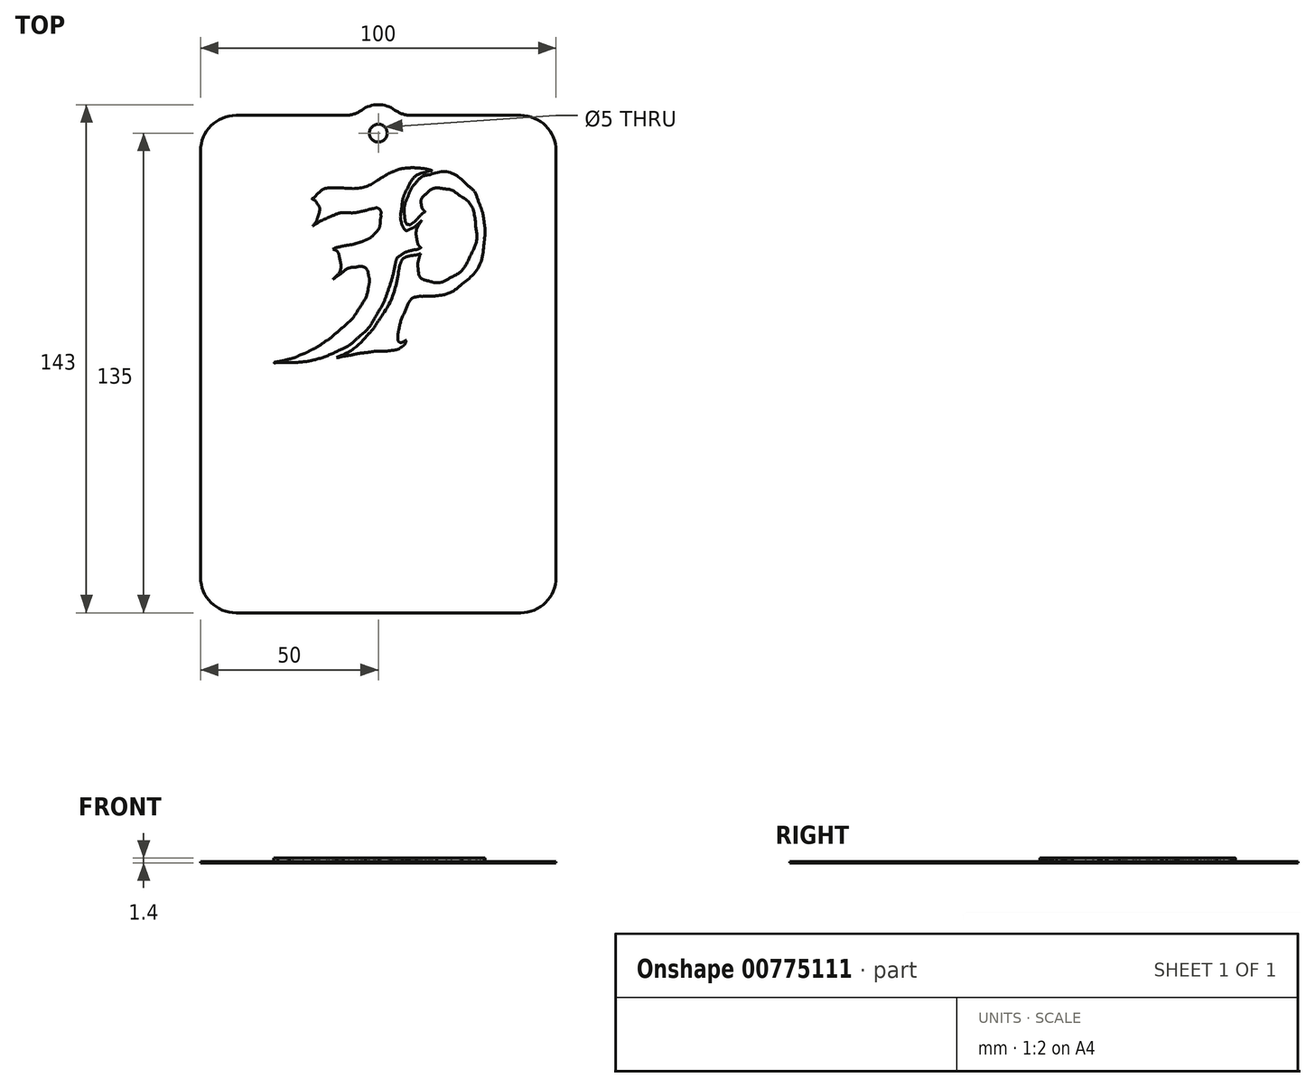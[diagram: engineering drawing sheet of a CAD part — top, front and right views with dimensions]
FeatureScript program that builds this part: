
annotation { "Feature Type Name" : "Feature", "Feature Type Description" : "" }
export const myFeature = defineFeature(function(context is Context, id is Id, definition is map)
    precondition{}
    {
        {
            var Q0;
            Q0=qCreatedBy(makeId("Top.planeOp"),FACE);
            var sketch = newSketch(context, id + "F0", { "sketchPlane" : qUnion([Q0])});
            skLineSegment(sketch, "E0.bottom", {"start": v(-40, 70) * mm, "end": v(-9.33, 70) * mm});
            skLineSegment(sketch, "E0.top", {"start": v(-40, -70) * mm, "end": v(40, -70) * mm});
            skLineSegment(sketch, "E0.left", {"start": v(-50, 60) * mm, "end": v(-50, -60) * mm});
            skLineSegment(sketch, "E0.right", {"start": v(50, 60) * mm, "end": v(50, -60) * mm});
            skPoint(sketch, "E0.middle", {"position": v(0, 0) * mm});
            skCircle(sketch, "E1", {"center": v(0, 65) * mm, "radius": 2.5 * mm});
            skPoint(sketch, "E2.visualSharp", {"position": v(-50, 70) * mm});
            skArc(sketch, "E2.filletArc", {"start": v(-40, 70) * mm, "mid": v(-47.07, 67.07) * mm, "end": v(-50, 60) * mm});
            skPoint(sketch, "E3.visualSharp", {"position": v(50, 70) * mm});
            skArc(sketch, "E3.filletArc", {"start": v(50, 60) * mm, "mid": v(47.07, 67.07) * mm, "end": v(40, 70) * mm});
            skPoint(sketch, "E4.visualSharp", {"position": v(50, -70) * mm});
            skArc(sketch, "E4.filletArc", {"start": v(40, -70) * mm, "mid": v(47.07, -67.07) * mm, "end": v(50, -60) * mm});
            skPoint(sketch, "E5.visualSharp", {"position": v(-50, -70) * mm});
            skArc(sketch, "E5.filletArc", {"start": v(-50, -60) * mm, "mid": v(-47.07, -67.07) * mm, "end": v(-40, -70) * mm});
            skArc(sketch, "E6", {"start": v(-4.66, 71.5) * mm, "mid": v(0, 73) * mm, "end": v(4.66, 71.5) * mm});
            skArc(sketch, "E7.filletArc", {"start": v(-9.33, 70) * mm, "mid": v(-6.88, 70.38) * mm, "end": v(-4.66, 71.5) * mm});
            skLineSegment(sketch, "E8", {"start": v(40, 70) * mm, "end": v(9.33, 70) * mm});
            skArc(sketch, "E9.filletArc", {"start": v(4.66, 71.5) * mm, "mid": v(6.88, 70.38) * mm, "end": v(9.33, 70) * mm});
            skSolve(sketch);
        }
        {
            var Q0;
            Q0=qSketchRegion(id+"F0",true);
            extrude(context, id + "F1", {"entities" : qUnion([Q0]), "depth" : .4 * mm, "offsetDistance" : 25 * mm, "symmetric" : true});
        }
        {
            var Q0;
            Q0=makeQuery(id+"F1.opExtrude","CAP_FACE",FACE,{"disambiguationData":[OSD([sQuery(id+"F0.wireOp",EDGE,"E0.bottom"),sQuery(id+"F0.wireOp",EDGE,"E0.top"),sQuery(id+"F0.wireOp",EDGE,"E0.left"),sQuery(id+"F0.wireOp",EDGE,"E0.right"),sQuery(id+"F0.wireOp",EDGE,"E1"),sQuery(id+"F0.wireOp",EDGE,"E2.filletArc"),sQuery(id+"F0.wireOp",EDGE,"E3.filletArc"),sQuery(id+"F0.wireOp",EDGE,"E4.filletArc"),sQuery(id+"F0.wireOp",EDGE,"E5.filletArc"),sQuery(id+"F0.wireOp",EDGE,"E6"),sQuery(id+"F0.wireOp",EDGE,"E7.filletArc"),sQuery(id+"F0.wireOp",EDGE,"E8"),sQuery(id+"F0.wireOp",EDGE,"E9.filletArc")])],"isStart":false});
            var sketch = newSketch(context, id + "F2", { "sketchPlane" : qUnion([Q0])});
            skFitSpline(sketch, "E10", {"points": [v(10.1, 55.33) * mm, v(10.4, 55.2) * mm, v(10.72, 55.22) * mm, v(11.03, 55.2) * mm]});
            skFitSpline(sketch, "E11", {"points": [v(11.03, 55.2) * mm, v(12.3, 55.1) * mm, v(13.56, 54.92) * mm, v(14.79, 54.6) * mm]});
            skFitSpline(sketch, "E12", {"points": [v(14.79, 54.6) * mm, v(14.9, 54.58) * mm, v(15.03, 54.59) * mm, v(15.1, 54.42) * mm]});
            skFitSpline(sketch, "E13", {"points": [v(15.1, 54.42) * mm, v(14.4, 54.4) * mm, v(13.76, 54.2) * mm, v(13.12, 53.98) * mm]});
            skFitSpline(sketch, "E14", {"points": [v(13.12, 53.98) * mm, v(10.8, 53.17) * mm, v(9.24, 51.53) * mm, v(8.14, 49.38) * mm]});
            skFitSpline(sketch, "E15", {"points": [v(8.14, 49.38) * mm, v(7.37, 47.87) * mm, v(6.84, 46.27) * mm, v(6.63, 44.6) * mm]});
            skFitSpline(sketch, "E16", {"points": [v(6.63, 44.6) * mm, v(6.43, 42.98) * mm, v(6.2, 41.35) * mm, v(6.52, 39.72) * mm]});
            skFitSpline(sketch, "E17", {"points": [v(6.52, 39.72) * mm, v(6.57, 39.43) * mm, v(6.65, 39.15) * mm, v(6.8, 38.88) * mm]});
            skFitSpline(sketch, "E18", {"points": [v(6.8, 38.88) * mm, v(7.2, 38.14) * mm, v(7.82, 37.59) * mm, v(8.94, 38.03) * mm]});
            skFitSpline(sketch, "E19", {"points": [v(8.94, 38.03) * mm, v(9.92, 38.4) * mm, v(10.73, 39.03) * mm, v(11.49, 39.74) * mm]});
            skFitSpline(sketch, "E20", {"points": [v(11.49, 39.74) * mm, v(11.7, 39.93) * mm, v(11.87, 40.14) * mm, v(12.1, 40.4) * mm]});
            skFitSpline(sketch, "E21", {"points": [v(12.1, 40.4) * mm, v(12.11, 40.2) * mm, v(12, 40.11) * mm, v(11.95, 40.02) * mm]});
            skFitSpline(sketch, "E22", {"points": [v(11.95, 40.02) * mm, v(10.86, 38.25) * mm, v(10.65, 36.34) * mm, v(11, 34.33) * mm]});
            skFitSpline(sketch, "E23", {"points": [v(11, 34.33) * mm, v(11.1, 33.86) * mm, v(11.3, 33.44) * mm, v(11.66, 33.1) * mm]});
            skFitSpline(sketch, "E24", {"points": [v(11.66, 33.1) * mm, v(12.01, 32.76) * mm, v(12, 32.75) * mm, v(11.54, 32.55) * mm]});
            skFitSpline(sketch, "E25", {"points": [v(11.54, 32.55) * mm, v(10.9, 32.27) * mm, v(10.2, 32.2) * mm, v(9.52, 32.03) * mm]});
            skFitSpline(sketch, "E26", {"points": [v(9.52, 32.03) * mm, v(8.35, 31.74) * mm, v(7.24, 31.29) * mm, v(6.24, 30.59) * mm]});
            skFitSpline(sketch, "E27", {"points": [v(6.24, 30.59) * mm, v(5.4, 30) * mm, v(4.98, 29.14) * mm, v(4.78, 28.18) * mm]});
            skFitSpline(sketch, "E28", {"points": [v(4.78, 28.18) * mm, v(4.29, 25.78) * mm, v(3.65, 23.42) * mm, v(2.86, 21.1) * mm]});
            skFitSpline(sketch, "E29", {"points": [v(2.86, 21.1) * mm, v(2.18, 19.1) * mm, v(1.4, 17.13) * mm, v(0.35, 15.3) * mm]});
            skFitSpline(sketch, "E30", {"points": [v(0.35, 15.3) * mm, v(-1.13, 12.75) * mm, v(-2.67, 10.25) * mm, v(-4.86, 8.23) * mm]});
            skFitSpline(sketch, "E31", {"points": [v(-4.86, 8.23) * mm, v(-6.57, 6.66) * mm, v(-8.36, 5.17) * mm, v(-10.46, 4.16) * mm]});
            skFitSpline(sketch, "E32", {"points": [v(-10.46, 4.16) * mm, v(-13.06, 2.91) * mm, v(-15.74, 1.83) * mm, v(-18.53, 1.11) * mm]});
            skFitSpline(sketch, "E33", {"points": [v(-18.53, 1.11) * mm, v(-19.7, 0.81) * mm, v(-20.9, 0.68) * mm, v(-22.09, 0.56) * mm]});
            skFitSpline(sketch, "E34", {"points": [v(-22.09, 0.56) * mm, v(-23.04, 0.46) * mm, v(-24, 0.4) * mm, v(-24.95, 0.4) * mm]});
            skFitSpline(sketch, "E35", {"points": [v(-26.63, 0.4) * mm, v(-26.77, 0.4) * mm, v(-26.91, 0.4) * mm, v(-27.05, 0.4) * mm]});
            skFitSpline(sketch, "E36", {"points": [v(-29.43, 0.48) * mm, v(-28.15, 0.72) * mm, v(-26.87, 0.96) * mm, v(-25.61, 1.3) * mm]});
            skFitSpline(sketch, "E37", {"points": [v(-25.61, 1.3) * mm, v(-25.1, 1.42) * mm, v(-24.59, 1.52) * mm, v(-24.09, 1.67) * mm]});
            skFitSpline(sketch, "E38", {"points": [v(-24.09, 1.67) * mm, v(-23.09, 1.97) * mm, v(-22.19, 2.52) * mm, v(-21.2, 2.87) * mm]});
            skFitSpline(sketch, "E39", {"points": [v(-21.2, 2.87) * mm, v(-20.16, 3.24) * mm, v(-19.2, 3.81) * mm, v(-18.21, 4.3) * mm]});
            skFitSpline(sketch, "E40", {"points": [v(-18.21, 4.3) * mm, v(-16.92, 4.96) * mm, v(-15.76, 5.8) * mm, v(-14.56, 6.58) * mm]});
            skFitSpline(sketch, "E41", {"points": [v(-14.56, 6.58) * mm, v(-13.45, 7.32) * mm, v(-12.44, 8.2) * mm, v(-11.43, 9.09) * mm]});
            skFitSpline(sketch, "E42", {"points": [v(-11.43, 9.09) * mm, v(-9.34, 10.92) * mm, v(-7.3, 12.82) * mm, v(-5.74, 15.18) * mm]});
            skFitSpline(sketch, "E43", {"points": [v(-5.74, 15.18) * mm, v(-4.42, 17.2) * mm, v(-3.27, 19.3) * mm, v(-2.77, 21.72) * mm]});
            skFitSpline(sketch, "E44", {"points": [v(-2.77, 21.72) * mm, v(-2.57, 22.7) * mm, v(-2.47, 23.74) * mm, v(-2.72, 24.7) * mm]});
            skFitSpline(sketch, "E45", {"points": [v(-2.72, 24.7) * mm, v(-3.22, 26.66) * mm, v(-4.56, 27.47) * mm, v(-6.5, 27.23) * mm]});
            skFitSpline(sketch, "E46", {"points": [v(-6.5, 27.23) * mm, v(-8.44, 27) * mm, v(-9.99, 25.93) * mm, v(-11.5, 24.8) * mm]});
            skFitSpline(sketch, "E47", {"points": [v(-11.5, 24.8) * mm, v(-11.87, 24.53) * mm, v(-12.22, 24.25) * mm, v(-12.58, 23.97) * mm]});
            skFitSpline(sketch, "E48", {"points": [v(-12.58, 23.97) * mm, v(-12.63, 24.07) * mm, v(-12.57, 24.1) * mm, v(-12.55, 24.12) * mm]});
            skFitSpline(sketch, "E49", {"points": [v(-12.55, 24.12) * mm, v(-10.9, 25.86) * mm, v(-10.5, 27.93) * mm, v(-11, 30.22) * mm]});
            skFitSpline(sketch, "E50", {"points": [v(-11, 30.22) * mm, v(-11.22, 31.21) * mm, v(-11.8, 31.93) * mm, v(-12.78, 32.35) * mm]});
            skFitSpline(sketch, "E51", {"points": [v(-12.78, 32.35) * mm, v(-12.15, 32.69) * mm, v(-11.5, 32.88) * mm, v(-10.84, 33.02) * mm]});
            skFitSpline(sketch, "E52", {"points": [v(-10.84, 33.02) * mm, v(-9.2, 33.39) * mm, v(-7.52, 33.62) * mm, v(-5.9, 34.09) * mm]});
            skFitSpline(sketch, "E53", {"points": [v(-5.9, 34.09) * mm, v(-5.03, 34.33) * mm, v(-4.2, 34.64) * mm, v(-3.37, 35) * mm]});
            skFitSpline(sketch, "E54", {"points": [v(-3.37, 35) * mm, v(-2.4, 35.43) * mm, v(-1.6, 36.08) * mm, v(-0.89, 36.86) * mm]});
            skFitSpline(sketch, "E55", {"points": [v(-0.89, 36.86) * mm, v(0.02, 37.85) * mm, v(0.46, 39.04) * mm, v(0.57, 40.38) * mm]});
            skFitSpline(sketch, "E56", {"points": [v(0.57, 40.38) * mm, v(0.61, 40.94) * mm, v(0.74, 41.5) * mm, v(0.7, 42.07) * mm]});
            skFitSpline(sketch, "E57", {"points": [v(0.7, 42.07) * mm, v(0.64, 43.16) * mm, v(-0.32, 43.94) * mm, v(-1.38, 43.77) * mm]});
            skFitSpline(sketch, "E58", {"points": [v(-1.38, 43.77) * mm, v(-2.44, 43.6) * mm, v(-3.48, 43.26) * mm, v(-4.53, 43.03) * mm]});
            skFitSpline(sketch, "E59", {"points": [v(-4.53, 43.03) * mm, v(-5.8, 42.75) * mm, v(-7.08, 42.56) * mm, v(-8.38, 42.58) * mm]});
            skFitSpline(sketch, "E60", {"points": [v(-8.38, 42.58) * mm, v(-10.34, 42.62) * mm, v(-12.17, 42.07) * mm, v(-13.95, 41.3) * mm]});
            skFitSpline(sketch, "E61", {"points": [v(-13.95, 41.3) * mm, v(-15.43, 40.68) * mm, v(-16.86, 39.94) * mm, v(-18.18, 39) * mm]});
            skFitSpline(sketch, "E62", {"points": [v(-18.18, 39) * mm, v(-18.24, 38.96) * mm, v(-18.3, 38.88) * mm, v(-18.43, 38.92) * mm]});
            skFitSpline(sketch, "E63", {"points": [v(-18.43, 38.92) * mm, v(-17.81, 39.62) * mm, v(-17.36, 40.41) * mm, v(-17.08, 41.27) * mm]});
            skFitSpline(sketch, "E64", {"points": [v(-17.08, 41.27) * mm, v(-16.6, 42.73) * mm, v(-16.57, 44.19) * mm, v(-17.45, 45.55) * mm]});
            skFitSpline(sketch, "E65", {"points": [v(-17.45, 45.55) * mm, v(-17.75, 46.02) * mm, v(-18.2, 46.27) * mm, v(-18.7, 46.56) * mm]});
            skFitSpline(sketch, "E66", {"points": [v(-18.7, 46.56) * mm, v(-17.86, 47.04) * mm, v(-17.27, 47.78) * mm, v(-16.56, 48.37) * mm]});
            skFitSpline(sketch, "E67", {"points": [v(-16.56, 48.37) * mm, v(-15.5, 49.26) * mm, v(-14.24, 49.56) * mm, v(-12.91, 49.6) * mm]});
            skFitSpline(sketch, "E68", {"points": [v(-12.91, 49.6) * mm, v(-11.9, 49.62) * mm, v(-10.88, 49.57) * mm, v(-9.87, 49.54) * mm]});
            skFitSpline(sketch, "E69", {"points": [v(-9.87, 49.54) * mm, v(-6.28, 49.43) * mm, v(-2.89, 50.17) * mm, v(0.23, 52.03) * mm]});
            skFitSpline(sketch, "E70", {"points": [v(0.23, 52.03) * mm, v(1.55, 52.82) * mm, v(2.87, 53.63) * mm, v(4.3, 54.22) * mm]});
            skFitSpline(sketch, "E71", {"points": [v(4.3, 54.22) * mm, v(5.65, 54.79) * mm, v(7.07, 55.1) * mm, v(8.53, 55.2) * mm]});
            skFitSpline(sketch, "E72", {"points": [v(8.53, 55.2) * mm, v(8.75, 55.21) * mm, v(8.98, 55.21) * mm, v(9.18, 55.33) * mm]});
            skFitSpline(sketch, "E73", {"points": [v(9.18, 55.33) * mm, v(9.2, 55.33) * mm, v(9.23, 55.33) * mm, v(9.25, 55.33) * mm]});
            skFitSpline(sketch, "E74", {"points": [v(9.95, 55.33) * mm, v(10, 55.33) * mm, v(10.05, 55.33) * mm, v(10.1, 55.33) * mm]});
            skFitSpline(sketch, "E75", {"points": [v(30, 35.94) * mm, v(29.82, 35.5) * mm, v(29.87, 35.05) * mm, v(29.8, 34.6) * mm]});
            skFitSpline(sketch, "E76", {"points": [v(29.8, 34.6) * mm, v(29.15, 29.83) * mm, v(27.18, 25.75) * mm, v(23.53, 22.6) * mm]});
            skFitSpline(sketch, "E77", {"points": [v(23.53, 22.6) * mm, v(21.48, 20.82) * mm, v(19.1, 19.7) * mm, v(16.43, 19.27) * mm]});
            skFitSpline(sketch, "E78", {"points": [v(16.43, 19.27) * mm, v(15.28, 19.08) * mm, v(14.1, 19.13) * mm, v(12.94, 19.09) * mm]});
            skFitSpline(sketch, "E79", {"points": [v(12.94, 19.09) * mm, v(12.19, 19.06) * mm, v(11.43, 19.06) * mm, v(10.68, 18.9) * mm]});
            skFitSpline(sketch, "E80", {"points": [v(10.68, 18.9) * mm, v(9.83, 18.73) * mm, v(9.19, 18.27) * mm, v(8.71, 17.55) * mm]});
            skFitSpline(sketch, "E81", {"points": [v(8.71, 17.55) * mm, v(8.55, 17.32) * mm, v(8.4, 17.08) * mm, v(8.3, 16.82) * mm]});
            skFitSpline(sketch, "E82", {"points": [v(8.3, 16.82) * mm, v(7.28, 14.4) * mm, v(6.28, 11.98) * mm, v(5.71, 9.41) * mm]});
            skFitSpline(sketch, "E83", {"points": [v(5.71, 9.41) * mm, v(5.58, 8.8) * mm, v(5.5, 8.18) * mm, v(5.54, 7.55) * mm]});
            skFitSpline(sketch, "E84", {"points": [v(5.54, 7.55) * mm, v(5.6, 6.54) * mm, v(6.29, 6.06) * mm, v(7.22, 6.4) * mm]});
            skFitSpline(sketch, "E85", {"points": [v(7.22, 6.4) * mm, v(7.42, 6.48) * mm, v(7.62, 6.57) * mm, v(7.85, 6.68) * mm]});
            skFitSpline(sketch, "E86", {"points": [v(7.85, 6.68) * mm, v(7.66, 5.99) * mm, v(7.35, 5.44) * mm, v(6.8, 5.02) * mm]});
            skFitSpline(sketch, "E87", {"points": [v(6.8, 5.02) * mm, v(5.85, 4.3) * mm, v(4.76, 3.97) * mm, v(3.6, 3.82) * mm]});
            skFitSpline(sketch, "E88", {"points": [v(3.6, 3.82) * mm, v(2.44, 3.67) * mm, v(1.28, 3.65) * mm, v(0.11, 3.61) * mm]});
            skFitSpline(sketch, "E89", {"points": [v(0.11, 3.61) * mm, v(-1.14, 3.57) * mm, v(-2.37, 3.38) * mm, v(-3.6, 3.23) * mm]});
            skFitSpline(sketch, "E90", {"points": [v(-3.6, 3.23) * mm, v(-5.73, 2.96) * mm, v(-7.8, 2.5) * mm, v(-9.92, 2.18) * mm]});
            skFitSpline(sketch, "E91", {"points": [v(-9.92, 2.18) * mm, v(-10.5, 2.1) * mm, v(-11.04, 1.9) * mm, v(-11.62, 1.83) * mm]});
            skFitSpline(sketch, "E92", {"points": [v(-11.77, 1.9) * mm, v(-8.29, 3.46) * mm, v(-5.3, 5.7) * mm, v(-2.71, 8.52) * mm]});
            skFitSpline(sketch, "E93", {"points": [v(-2.71, 8.52) * mm, v(-1.4, 9.95) * mm, v(-0.37, 11.54) * mm, v(0.65, 13.17) * mm]});
            skFitSpline(sketch, "E94", {"points": [v(0.65, 13.17) * mm, v(3.21, 17.28) * mm, v(4.83, 21.77) * mm, v(5.8, 26.51) * mm]});
            skFitSpline(sketch, "E95", {"points": [v(5.8, 26.51) * mm, v(5.93, 27.12) * mm, v(5.98, 27.75) * mm, v(6.26, 28.32) * mm]});
            skFitSpline(sketch, "E96", {"points": [v(6.26, 28.32) * mm, v(6.88, 29.6) * mm, v(7.97, 30.22) * mm, v(9.29, 30.53) * mm]});
            skFitSpline(sketch, "E97", {"points": [v(9.29, 30.53) * mm, v(9.52, 30.6) * mm, v(9.77, 30.6) * mm, v(10.01, 30.64) * mm]});
            skFitSpline(sketch, "E98", {"points": [v(10.01, 30.64) * mm, v(10.61, 30.72) * mm, v(11.2, 30.84) * mm, v(11.77, 31.12) * mm]});
            skFitSpline(sketch, "E99", {"points": [v(11.77, 31.12) * mm, v(11.8, 30.83) * mm, v(11.66, 30.62) * mm, v(11.6, 30.38) * mm]});
            skFitSpline(sketch, "E100", {"points": [v(11.6, 30.38) * mm, v(11.27, 29.13) * mm, v(11.08, 27.86) * mm, v(11.26, 26.56) * mm]});
            skFitSpline(sketch, "E101", {"points": [v(11.26, 26.56) * mm, v(11.5, 24.84) * mm, v(12.51, 23.84) * mm, v(14.16, 23.44) * mm]});
            skFitSpline(sketch, "E102", {"points": [v(14.16, 23.44) * mm, v(16.43, 22.88) * mm, v(18.55, 23.34) * mm, v(20.55, 24.47) * mm]});
            skFitSpline(sketch, "E103", {"points": [v(20.55, 24.47) * mm, v(22.99, 25.85) * mm, v(24.64, 27.97) * mm, v(25.87, 30.46) * mm]});
            skFitSpline(sketch, "E104", {"points": [v(25.87, 30.46) * mm, v(27.07, 32.92) * mm, v(27.75, 35.52) * mm, v(27.45, 38.26) * mm]});
            skFitSpline(sketch, "E105", {"points": [v(27.45, 38.26) * mm, v(27.05, 41.89) * mm, v(25.82, 45.16) * mm, v(22.85, 47.47) * mm]});
            skFitSpline(sketch, "E106", {"points": [v(22.85, 47.47) * mm, v(21.73, 48.34) * mm, v(20.48, 49.04) * mm, v(19.06, 49.25) * mm]});
            skFitSpline(sketch, "E107", {"points": [v(19.06, 49.25) * mm, v(16.96, 49.57) * mm, v(14.97, 49.26) * mm, v(13.33, 47.78) * mm]});
            skFitSpline(sketch, "E108", {"points": [v(13.33, 47.78) * mm, v(12.27, 46.82) * mm, v(12.02, 45.54) * mm, v(12.22, 44.15) * mm]});
            skFitSpline(sketch, "E109", {"points": [v(12.22, 44.15) * mm, v(12.25, 43.92) * mm, v(12.4, 43.72) * mm, v(12.57, 43.55) * mm]});
            skFitSpline(sketch, "E110", {"points": [v(12.57, 43.55) * mm, v(12.78, 43.32) * mm, v(13, 43.09) * mm, v(13.23, 42.85) * mm]});
            skFitSpline(sketch, "E111", {"points": [v(13.23, 42.85) * mm, v(12.52, 42.5) * mm, v(11.97, 41.95) * mm, v(11.43, 41.38) * mm]});
            skFitSpline(sketch, "E112", {"points": [v(11.43, 41.38) * mm, v(10.78, 40.68) * mm, v(10.1, 40.02) * mm, v(9.31, 39.48) * mm]});
            skFitSpline(sketch, "E113", {"points": [v(9.31, 39.48) * mm, v(8.95, 39.24) * mm, v(8.58, 39.27) * mm, v(8.2, 39.29) * mm]});
            skFitSpline(sketch, "E114", {"points": [v(8.2, 39.29) * mm, v(8.03, 39.3) * mm, v(7.95, 39.48) * mm, v(7.86, 39.61) * mm]});
            skFitSpline(sketch, "E115", {"points": [v(7.86, 39.61) * mm, v(7.65, 39.94) * mm, v(7.55, 40.3) * mm, v(7.51, 40.68) * mm]});
            skFitSpline(sketch, "E116", {"points": [v(7.51, 40.68) * mm, v(7.28, 42.97) * mm, v(7.54, 45.2) * mm, v(8.38, 47.35) * mm]});
            skFitSpline(sketch, "E117", {"points": [v(8.38, 47.35) * mm, v(8.91, 48.7) * mm, v(9.6, 49.96) * mm, v(10.56, 51.03) * mm]});
            skFitSpline(sketch, "E118", {"points": [v(10.56, 51.03) * mm, v(11.63, 52.22) * mm, v(12.92, 53.02) * mm, v(14.48, 53.34) * mm]});
            skFitSpline(sketch, "E119", {"points": [v(14.48, 53.34) * mm, v(18.64, 54.18) * mm, v(22.2, 52.92) * mm, v(25.3, 50.12) * mm]});
            skFitSpline(sketch, "E120", {"points": [v(25.3, 50.12) * mm, v(27, 48.59) * mm, v(27.9, 46.55) * mm, v(28.67, 44.45) * mm]});
            skFitSpline(sketch, "E121", {"points": [v(28.67, 44.45) * mm, v(29.3, 42.73) * mm, v(29.63, 40.94) * mm, v(29.86, 39.12) * mm]});
            skFitSpline(sketch, "E122", {"points": [v(29.86, 39.12) * mm, v(29.89, 38.93) * mm, v(29.87, 38.73) * mm, v(30, 38.57) * mm]});
            skFitSpline(sketch, "E123", {"points": [v(30, 38.57) * mm, v(30, 38.3) * mm, v(30, 38.04) * mm, v(30, 37.78) * mm]});
            skFitSpline(sketch, "E124", {"points": [v(30, 36.86) * mm, v(30, 36.74) * mm, v(30, 36.62) * mm, v(30, 36.5) * mm]});
            skFitSpline(sketch, "E125", {"points": [v(30, 36.36) * mm, v(30, 36.22) * mm, v(30, 36.08) * mm, v(30, 35.94) * mm]});
            skFitSpline(sketch, "E126", {"points": [v(-29.43, 0.48) * mm, v(-29.07, 0.33) * mm, v(-28.68, 0.46) * mm, v(-28.31, 0.4) * mm]});
            skFitSpline(sketch, "E127", {"points": [v(-24.95, 0.4) * mm, v(-25.28, 0.4) * mm, v(-25.6, 0.4) * mm, v(-25.93, 0.4) * mm]});
            skFitSpline(sketch, "E128", {"points": [v(30, 37.78) * mm, v(30, 37.48) * mm, v(30, 37.17) * mm, v(30, 36.86) * mm]});
            skFitSpline(sketch, "E129", {"points": [v(9.25, 55.33) * mm, v(9.49, 55.33) * mm, v(9.72, 55.33) * mm, v(9.95, 55.33) * mm]});
            skFitSpline(sketch, "E130", {"points": [v(-25.93, 0.4) * mm, v(-26.17, 0.4) * mm, v(-26.4, 0.4) * mm, v(-26.63, 0.4) * mm]});
            skFitSpline(sketch, "E131", {"points": [v(30, 36.5) * mm, v(30, 36.46) * mm, v(30, 36.41) * mm, v(30, 36.36) * mm]});
            skFitSpline(sketch, "E132", {"points": [v(-11.77, 1.9) * mm, v(-11.72, 1.87) * mm, v(-11.67, 1.85) * mm, v(-11.62, 1.83) * mm]});
            skLineSegment(sketch, "E133", {"start": v(-27.05, 0.4) * mm, "end": v(-28.31, 0.4) * mm});
            skSolve(sketch);
        }
        {
            var Q0;
            Q0=qSketchRegion(id+"F2",true);
            extrude(context, id + "F3", {"entities" : qUnion([Q0]), "operationType" : NewBodyOperationType.ADD, "depth" : 1 * mm, "offsetDistance" : 25 * mm});
        }
    });
